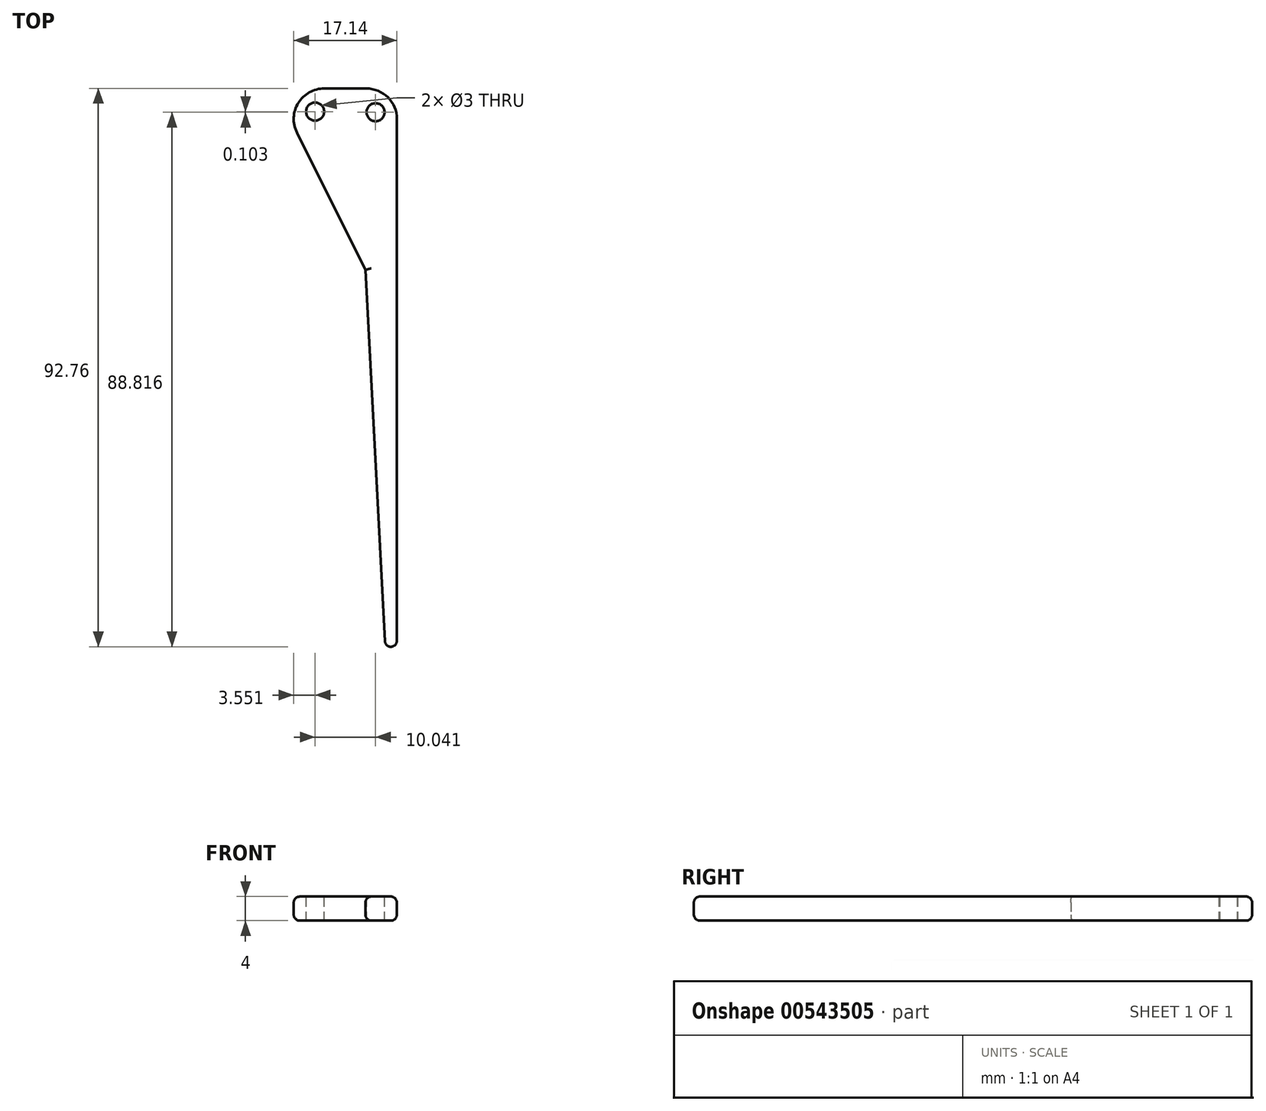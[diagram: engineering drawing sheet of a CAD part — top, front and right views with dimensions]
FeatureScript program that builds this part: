
annotation { "Feature Type Name" : "Feature", "Feature Type Description" : "" }
export const myFeature = defineFeature(function(context is Context, id is Id, definition is map)
    precondition{}
    {
        {
            var Q0;
            Q0=qCreatedBy(makeId("Top.planeOp"),FACE);
            var sketch = newSketch(context, id + "F0", { "sketchPlane" : qUnion([Q0])});
            skLineSegment(sketch, "E0", {"start": v(0, 0) * mm, "end": v(0, -130) * mm});
            skLineSegment(sketch, "E1", {"start": v(0, -130) * mm, "end": v(-5.23, -30.14) * mm});
            skLineSegment(sketch, "E2", {"start": v(0, 0) * mm, "end": v(-20.28, 0) * mm});
            skLineSegment(sketch, "E3", {"start": v(-5.23, -30.14) * mm, "end": v(-20.28, 0) * mm});
            skSolve(sketch);
        }
        {
            var Q0;
            Q0 = qSketchRegion(id + "F0", true);
            extrude(context, id + "F1", {"entities" : qUnion([Q0]), "depth" : 4 * mm, "offsetDistance" : 25.4 * mm});
        }
        {
            var Q0;
            Q0=makeQuery(id+"F1.opExtrude","SWEPT_EDGE",EDGE,{"disambiguationData":[OSD([sQuery(id+"F0.wireOp",EDGE,"E0"),sQuery(id+"F0.wireOp",EDGE,"E2")])]});
            fillet(context, id + "F2", {"entities" : qUnion([Q0]), "radius" : 5.08 * mm, "tangentPropagation" : true, "allowEdgeOverflow" : false});
        }
        {
            var Q0;
            Q0=makeQuery(id+"F1.opExtrude","SWEPT_EDGE",EDGE,{"disambiguationData":[OSD([sQuery(id+"F0.wireOp",EDGE,"E2"),sQuery(id+"F0.wireOp",EDGE,"E3")])]});
            fillet(context, id + "F3", {"entities" : qUnion([Q0]), "radius" : 5.08 * mm, "tangentPropagation" : true, "allowEdgeOverflow" : false});
        }
        {
            var Q0;
            Q0=makeQuery(id+"F1.opExtrude","SWEPT_EDGE",EDGE,{"disambiguationData":[OSD([sQuery(id+"F0.wireOp",EDGE,"E0"),sQuery(id+"F0.wireOp",EDGE,"E1")])]});
            fillet(context, id + "F4", {"entities" : qUnion([Q0]), "radius" : 1 * mm, "tangentPropagation" : true, "allowEdgeOverflow" : false});
        }
        {
            var Q0;
            Q0=makeQuery(id+"F1.opExtrude","CAP_EDGE",EDGE,{"disambiguationData":[OSD([sQuery(id+"F0.wireOp",EDGE,"E3")])],"isStart":false});
            var Q1;
            Q1=makeQuery(id+"F1.opExtrude","CAP_EDGE",EDGE,{"disambiguationData":[OSD([sQuery(id+"F0.wireOp",EDGE,"E1")])],"isStart":false});
            fillet(context, id + "F5", {"entities" : qUnion([Q0, Q1]), "radius" : 1 * mm, "tangentPropagation" : true, "allowEdgeOverflow" : false});
        }
        {
            var Q0;
            Q0=makeQuery(id+"F1.opExtrude","CAP_FACE",FACE,{"disambiguationData":[OSD([sQuery(id+"F0.wireOp",EDGE,"E0"),sQuery(id+"F0.wireOp",EDGE,"E1"),sQuery(id+"F0.wireOp",EDGE,"E2"),sQuery(id+"F0.wireOp",EDGE,"E3")])],"isStart":false});
            var sketch = newSketch(context, id + "F6", { "sketchPlane" : qUnion([Q0])});
            skCircle(sketch, "E4", {"center": v(-13.59, -3.84) * mm, "radius": 1.5 * mm});
            skCircle(sketch, "E5", {"center": v(-3.55, -3.94) * mm, "radius": 1.5 * mm});
            skSolve(sketch);
        }
        {
            var Q0;
            Q0=makeQuery(id+"F6.imprint","IMPRINT",FACE,{"disambiguationData":[TD([[makeQuery(id+"F6.imprint","IMPRINT",EDGE,{"derivedFrom":sQuery(id+"F6.wireOp",EDGE,"E4")}),1.0]])]});
            var Q1;
            Q1=makeQuery(id+"F6.imprint","IMPRINT",FACE,{"disambiguationData":[TD([[makeQuery(id+"F6.imprint","IMPRINT",EDGE,{"derivedFrom":sQuery(id+"F6.wireOp",EDGE,"QIF3phVv-AMyp-qU4d-SI5N-LPUeLnqHj8zp")}),1.0]])]});
            var Q2;
            Q2=makeQuery(id+"F6.imprint","IMPRINT",FACE,{"disambiguationData":[TD([[makeQuery(id+"F6.imprint","IMPRINT",EDGE,{"derivedFrom":sQuery(id+"F6.wireOp",EDGE,"E5")}),1.0]])]});
            extrude(context, id + "F7", {"entities" : qUnion([Q0, Q1, Q2]), "operationType" : NewBodyOperationType.REMOVE, "oppositeDirection" : true, "depth" : 25.4 * mm, "offsetDistance" : 25.4 * mm});
        }
        {
            var Q0;
            Q0=makeQuery(id+"F1.opExtrude","CAP_EDGE",EDGE,{"disambiguationData":[OSD([sQuery(id+"F0.wireOp",EDGE,"E2")])],"isStart":true});
            var Q1;
            Q1=makeQuery(id+"F1.opExtrude","CAP_EDGE",EDGE,{"disambiguationData":[OSD([sQuery(id+"F0.wireOp",EDGE,"E3")])],"isStart":true});
            fillet(context, id + "F8", {"entities" : qUnion([Q0, Q1]), "radius" : 1 * mm, "tangentPropagation" : true, "allowEdgeOverflow" : false});
        }
    });
